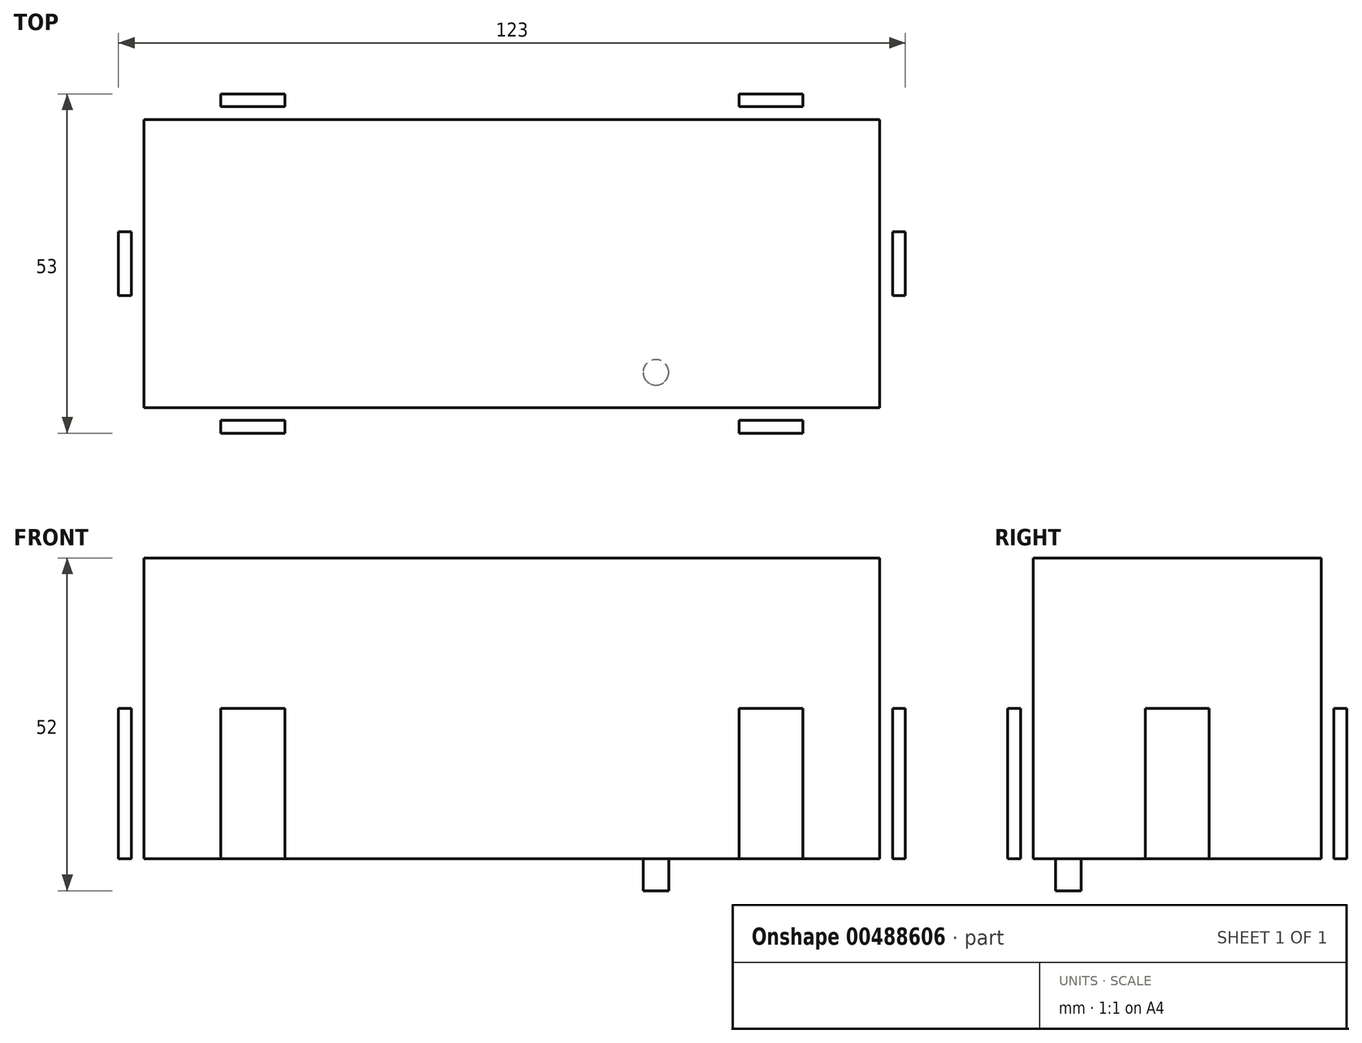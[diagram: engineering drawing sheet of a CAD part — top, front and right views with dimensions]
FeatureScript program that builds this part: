
annotation { "Feature Type Name" : "Feature", "Feature Type Description" : "" }
export const myFeature = defineFeature(function(context is Context, id is Id, definition is map)
    precondition{}
    {
        {
            var Q0;
            Q0=qCreatedBy(makeId("Top.planeOp"),FACE);
            var sketch = newSketch(context, id + "F0", { "sketchPlane" : qUnion([Q0])});
            skLineSegment(sketch, "E0.bottom", {"start": v(0, 0) * mm, "end": v(115, 0) * mm});
            skLineSegment(sketch, "E0.top", {"start": v(0, -45) * mm, "end": v(115, -45) * mm});
            skLineSegment(sketch, "E0.left", {"start": v(0, 0) * mm, "end": v(0, -45) * mm});
            skLineSegment(sketch, "E0.right", {"start": v(115, 0) * mm, "end": v(115, -45) * mm});
            skSolve(sketch);
        }
        {
            var Q0;
            Q0=qSketchRegion(id+"F0",true);
            extrude(context, id + "F1", {"entities" : qUnion([Q0]), "depth" : 47 * mm});
        }
        {
            var Q0;
            Q0=qCreatedBy(makeId("Top.planeOp"),FACE);
            var sketch = newSketch(context, id + "F2", { "sketchPlane" : qUnion([Q0])});
            skLineSegment(sketch, "E1.bottom", {"start": v(-4, 4) * mm, "end": v(119, 4) * mm});
            skLineSegment(sketch, "E1.top", {"start": v(-4, -49) * mm, "end": v(119, -49) * mm});
            skLineSegment(sketch, "E1.left", {"start": v(-4, 4) * mm, "end": v(-4, -49) * mm});
            skLineSegment(sketch, "E1.right", {"start": v(119, 4) * mm, "end": v(119, -49) * mm});
            skLineSegment(sketch, "E2", {"start": v(112.9, 0) * mm, "end": v(112.9, 4) * mm, "construction": true});
            skLineSegment(sketch, "E3", {"start": v(114.02, -49) * mm, "end": v(114.02, -45) * mm, "construction": true});
            skLineSegment(sketch, "E4", {"start": v(115, -22.5) * mm, "end": v(119, -22.5) * mm, "construction": true});
            skLineSegment(sketch, "E5", {"start": v(-4, -21.85) * mm, "end": v(0, -21.85) * mm, "construction": true});
            skPoint(sketch, "E6", {"position": v(119, -22.5) * mm});
            skSolve(sketch);
        }
        {
            var Q0;
            Q0=qSketchRegion(id+"F2",true);
            extrude(context, id + "F3", {"entities" : qUnion([Q0]), "oppositeDirection" : true, "depth" : 5 * mm});
        }
        {
            var Q0;
            Q0=makeQuery(id+"F3.opExtrude","CAP_FACE",FACE,{"disambiguationData":[OSD([sQuery(id+"F2.wireOp",EDGE,"E1.bottom"),sQuery(id+"F2.wireOp",EDGE,"E1.top"),sQuery(id+"F2.wireOp",EDGE,"E1.left"),sQuery(id+"F2.wireOp",EDGE,"E1.right")])],"isStart":true});
            var sketch = newSketch(context, id + "F4", { "sketchPlane" : qUnion([Q0])});
            skLineSegment(sketch, "E7.0", {"start": v(-4, 4) * mm, "end": v(119, 4) * mm});
            skLineSegment(sketch, "E8.0", {"start": v(119, 4) * mm, "end": v(119, -49) * mm});
            skLineSegment(sketch, "E9.0", {"start": v(-4, 4) * mm, "end": v(-4, -49) * mm});
            skLineSegment(sketch, "E10.0", {"start": v(-4, -49) * mm, "end": v(119, -49) * mm});
            skLineSegment(sketch, "E11.bottom", {"start": v(11.09, 28.37) * mm, "end": v(20, 28.37) * mm});
            skLineSegment(sketch, "E11.top", {"start": v(11.09, 26.28) * mm, "end": v(20, 26.28) * mm});
            skLineSegment(sketch, "E11.left", {"start": v(11.09, 28.37) * mm, "end": v(11.09, 26.28) * mm});
            skLineSegment(sketch, "E11.right", {"start": v(20, 28.37) * mm, "end": v(20, 26.28) * mm});
            skLineSegment(sketch, "E12.bottom", {"start": v(-2, 2) * mm, "end": v(117, 2) * mm});
            skLineSegment(sketch, "E12.top", {"start": v(-2, -47) * mm, "end": v(117, -47) * mm});
            skLineSegment(sketch, "E12.left", {"start": v(-2, 2) * mm, "end": v(-2, -47) * mm});
            skLineSegment(sketch, "E12.right", {"start": v(117, 2) * mm, "end": v(117, -47) * mm});
            skLineSegment(sketch, "E13", {"start": v(12, 4) * mm, "end": v(12, -49) * mm});
            skLineSegment(sketch, "E14", {"start": v(22, 4) * mm, "end": v(22, -49) * mm});
            skLineSegment(sketch, "E15", {"start": v(93, 4) * mm, "end": v(93, -49) * mm});
            skLineSegment(sketch, "E16", {"start": v(103, 4) * mm, "end": v(103, -49) * mm});
            skLineSegment(sketch, "E17", {"start": v(12, -14.4) * mm, "end": v(22, -14.4) * mm, "construction": true});
            skLineSegment(sketch, "E18", {"start": v(93, -17.68) * mm, "end": v(103, -17.68) * mm, "construction": true});
            skLineSegment(sketch, "E19", {"start": v(-4, -9.95) * mm, "end": v(12, -9.95) * mm, "construction": true});
            skLineSegment(sketch, "E20", {"start": v(103, -12.08) * mm, "end": v(119, -12.08) * mm, "construction": true});
            skLineSegment(sketch, "E21", {"start": v(-4, -17.5) * mm, "end": v(119, -17.5) * mm});
            skLineSegment(sketch, "E22", {"start": v(-4, -27.5) * mm, "end": v(119, -27.5) * mm});
            skLineSegment(sketch, "E23", {"start": v(60.65, -17.5) * mm, "end": v(60.65, -27.5) * mm, "construction": true});
            skLineSegment(sketch, "E24", {"start": v(73.6, 4) * mm, "end": v(73.6, -17.5) * mm, "construction": true});
            skLineSegment(sketch, "E25", {"start": v(74.56, -27.5) * mm, "end": v(74.56, -49) * mm, "construction": true});
            skSolve(sketch);
        }
        {
            var Q0;
            {var subQ0=sQuery(id+"F4.wireOp",EDGE,"E13");var subQ1=sQuery(id+"F4.wireOp",EDGE,"E7.0");var subQ2=makeQuery(id+"F4.imprint","INTERSECT",VERTEX,{"derivedFrom":[subQ1,subQ0]});Q0=makeQuery(id+"F4.imprint","IMPRINT",FACE,{"disambiguationData":[TD([[makeQuery(id+"F4.imprint","IMPRINT",EDGE,{"disambiguationData":[TD([[subQ2,-1.0]])],"derivedFrom":subQ1}),-1.0]])]});}
            var Q1;
            {var subQ0=sQuery(id+"F4.wireOp",EDGE,"E21");var subQ1=sQuery(id+"F4.wireOp",EDGE,"E9.0");var subQ2=makeQuery(id+"F4.imprint","INTERSECT",VERTEX,{"derivedFrom":[subQ1,subQ0]});Q1=makeQuery(id+"F4.imprint","IMPRINT",FACE,{"disambiguationData":[TD([[makeQuery(id+"F4.imprint","IMPRINT",EDGE,{"disambiguationData":[TD([[subQ2,-1.0]])],"derivedFrom":subQ1}),1.0]])]});}
            var Q2;
            {var subQ0=sQuery(id+"F4.wireOp",EDGE,"E13");var subQ1=sQuery(id+"F4.wireOp",EDGE,"E10.0");var subQ2=makeQuery(id+"F4.imprint","INTERSECT",VERTEX,{"derivedFrom":[subQ1,subQ0]});Q2=makeQuery(id+"F4.imprint","IMPRINT",FACE,{"disambiguationData":[TD([[makeQuery(id+"F4.imprint","IMPRINT",EDGE,{"disambiguationData":[TD([[subQ2,-1.0]])],"derivedFrom":subQ1}),1.0]])]});}
            var Q3;
            {var subQ0=sQuery(id+"F4.wireOp",EDGE,"E15");var subQ1=sQuery(id+"F4.wireOp",EDGE,"E10.0");var subQ2=makeQuery(id+"F4.imprint","INTERSECT",VERTEX,{"derivedFrom":[subQ1,subQ0]});Q3=makeQuery(id+"F4.imprint","IMPRINT",FACE,{"disambiguationData":[TD([[makeQuery(id+"F4.imprint","IMPRINT",EDGE,{"disambiguationData":[TD([[subQ2,-1.0]])],"derivedFrom":subQ1}),1.0]])]});}
            var Q4;
            {var subQ0=sQuery(id+"F4.wireOp",EDGE,"E15");var subQ1=sQuery(id+"F4.wireOp",EDGE,"E7.0");var subQ2=makeQuery(id+"F4.imprint","INTERSECT",VERTEX,{"derivedFrom":[subQ1,subQ0]});Q4=makeQuery(id+"F4.imprint","IMPRINT",FACE,{"disambiguationData":[TD([[makeQuery(id+"F4.imprint","IMPRINT",EDGE,{"disambiguationData":[TD([[subQ2,-1.0]])],"derivedFrom":subQ1}),-1.0]])]});}
            var Q5;
            {var subQ0=sQuery(id+"F4.wireOp",EDGE,"E21");var subQ1=sQuery(id+"F4.wireOp",EDGE,"E8.0");var subQ2=makeQuery(id+"F4.imprint","INTERSECT",VERTEX,{"derivedFrom":[subQ1,subQ0]});Q5=makeQuery(id+"F4.imprint","IMPRINT",FACE,{"disambiguationData":[TD([[makeQuery(id+"F4.imprint","IMPRINT",EDGE,{"disambiguationData":[TD([[subQ2,-1.0]])],"derivedFrom":subQ1}),-1.0]])]});}
            extrude(context, id + "F5", {"entities" : qUnion([Q0, Q1, Q2, Q3, Q4, Q5]), "operationType" : NewBodyOperationType.ADD, "depth" : 23.5 * mm});
        }
        {
            var Q0;
            Q0=makeQuery(id+"F3.opExtrude","CAP_FACE",FACE,{"disambiguationData":[OSD([sQuery(id+"F2.wireOp",EDGE,"E1.bottom"),sQuery(id+"F2.wireOp",EDGE,"E1.top"),sQuery(id+"F2.wireOp",EDGE,"E1.left"),sQuery(id+"F2.wireOp",EDGE,"E1.right")])],"isStart":false});
            var sketch = newSketch(context, id + "F6", { "sketchPlane" : qUnion([Q0])});
            skLineSegment(sketch, "E26.bottom", {"start": v(-14.63, 72.02) * mm, "end": v(6.59, 72.02) * mm});
            skLineSegment(sketch, "E26.top", {"start": v(-14.63, 53.02) * mm, "end": v(6.59, 53.02) * mm});
            skLineSegment(sketch, "E26.left", {"start": v(-14.63, 72.02) * mm, "end": v(-14.63, 53.02) * mm});
            skLineSegment(sketch, "E26.right", {"start": v(6.59, 72.02) * mm, "end": v(6.59, 53.02) * mm});
            skSolve(sketch);
        }
        {
            var Q0;
            Q0=makeQuery(id+"F6.imprint","IMPRINT",FACE,{"disambiguationData":[TD([[makeQuery(id+"F6.imprint","IMPRINT",EDGE,{"derivedFrom":makeQuery(id+"F3.opExtrude","CAP_EDGE",EDGE,{"disambiguationData":[OSD([sQuery(id+"F2.wireOp",EDGE,"E1.bottom")])],"isStart":false})}),1.0]])]});
            var sketch = newSketch(context, id + "F7", { "sketchPlane" : qUnion([Q0])});
            skPoint(sketch, "E27.0", {"position": v(57.5, 49) * mm});
            skLineSegment(sketch, "E28", {"start": v(57.5, 49) * mm, "end": v(57.5, -4) * mm, "construction": true});
            skLineSegment(sketch, "E29", {"start": v(57.5, 39.5) * mm, "end": v(-4.43, 39.5) * mm, "construction": true});
            skLineSegment(sketch, "E30", {"start": v(29, 49) * mm, "end": v(29, -4.14) * mm, "construction": true});
            skCircle(sketch, "E31", {"center": v(35, 39.5) * mm, "radius": 2 * mm});
            skCircle(sketch, "E32.MirrorC", {"center": v(80, 39.5) * mm, "radius": 2 * mm});
            skSolve(sketch);
        }
        {
            var Q0;
            Q0=makeQuery(id+"F7.imprint","IMPRINT",FACE,{"disambiguationData":[TD([[makeQuery(id+"F7.imprint","IMPRINT",EDGE,{"derivedFrom":sQuery(id+"F7.wireOp",EDGE,"E32.MirrorC")}),-1.0]])]});
            var Q1;
            Q1=makeQuery(id+"F7.imprint","IMPRINT",FACE,{"disambiguationData":[TD([[makeQuery(id+"F7.imprint","IMPRINT",EDGE,{"derivedFrom":sQuery(id+"F7.wireOp",EDGE,"E31")}),1.0]])]});
            var Q2;
            Q2=makeQuery(id+"F3.opExtrude","CAP_FACE",FACE,{"disambiguationData":[OSD([sQuery(id+"F2.wireOp",EDGE,"E1.bottom"),sQuery(id+"F2.wireOp",EDGE,"E1.top"),sQuery(id+"F2.wireOp",EDGE,"E1.left"),sQuery(id+"F2.wireOp",EDGE,"E1.right")])],"isStart":true});
            extrude(context, id + "F8", {"entities" : qUnion([Q0, Q1]), "operationType" : NewBodyOperationType.REMOVE, "endBound" : BoundingType.UP_TO_SURFACE, "oppositeDirection" : true, "endBoundEntityFace" : qUnion([Q2]), "depth" : 25 * mm});
        }
    });
